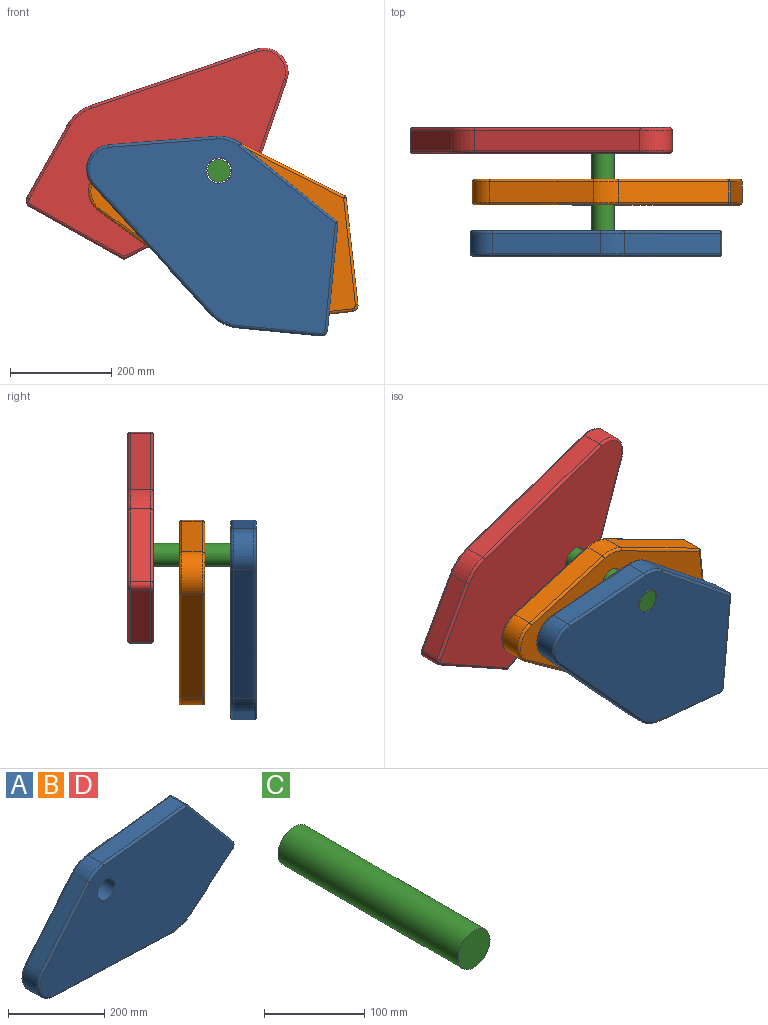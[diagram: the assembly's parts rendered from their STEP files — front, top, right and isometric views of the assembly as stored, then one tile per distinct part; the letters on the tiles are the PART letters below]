
ASSEMBLY  parts=4 mates=3
PART A: 33 faces, bbox 583.2x50.8x314.1 mm
  f0: plane 568.09x297.13mm, normal (0,-1,0), area 117364mm2, adj f10,f11,f12,f13,f14,f15,f16,f17
  f1: plane 568.09x297.13mm, normal (0,1,0), area 117364mm2, adj f10,f19,f20,f21,f22,f23,f24,f25
  f2: plane 163.02x136.69mm, normal (-0.77,0,0.64), area 8646mm2, adj f3,f9,f11,f19
  f3: cylinder r=48.03mm len=78.85mm, axis (0,1,0), area 4357.3mm2, adj f2,f4,f12,f20
  f4: plane 344.79x40.64mm, normal (-0.04,0,-1), area 14021.6mm2, adj f3,f5,f14,f22
  f5: cylinder r=83.11mm len=56.42mm, axis (0,1,0), area 2480mm2, adj f4,f6,f16,f24
  f6: plane 126.2x105.89mm, normal (0.64,0,-0.77), area 6695mm2, adj f5,f18,f26,f28
  f7: plane 162.25x136.14mm, normal (0.77,0,0.64), area 8607.4mm2, adj f17,f25,f28,f31
  f8: plane 242.51x40.64mm, normal (-0.12,0,0.99), area 9925.6mm2, adj f9,f15,f23,f31
  f9: cylinder r=68.26mm len=44.21mm, axis (0,1,0), area 2092.1mm2, adj f2,f8,f13,f21
  f10: cylinder r=25.4mm len=50.8mm, axis (0,-1,0), area 8107.3mm2, adj f0,f1
  f11: cylinder r=5.08mm len=166.29mm, axis (0.64,0,0.77), area 1697.6mm2, adj f0,f2,f12,f13
  f12: torus R=42.95mm, axis (0,-1,0), area 822.7mm2, adj f0,f3,f11,f14
  f13: torus R=63.18mm, axis (0,-1,0), area 399.7mm2, adj f0,f9,f11,f15
  f14: cylinder r=5.08mm len=344.98mm, axis (-1,0,0.04), area 2753.1mm2, adj f0,f4,f12,f16
  f15: cylinder r=5.08mm len=243.11mm, axis (0.99,0,0.12), area 1948.9mm2, adj f0,f8,f13,f32
  f16: torus R=78.03mm, axis (0,-1,0), area 476.1mm2, adj f0,f5,f14,f18
  f17: cylinder r=5.08mm len=165.51mm, axis (0.64,0,-0.77), area 1690.1mm2, adj f0,f7,f27,f32
  f18: cylinder r=5.08mm len=129.46mm, axis (-0.77,0,-0.64), area 1314.6mm2, adj f0,f6,f16,f27
  f19: cylinder r=5.08mm len=166.29mm, axis (-0.64,0,-0.77), area 1697.6mm2, adj f1,f2,f20,f21
  f20: torus R=42.95mm, axis (0,-1,0), area 822.7mm2, adj f1,f3,f19,f22
  f21: torus R=63.18mm, axis (0,-1,0), area 399.7mm2, adj f1,f9,f19,f23
  f22: cylinder r=5.08mm len=344.98mm, axis (1,0,-0.04), area 2753.1mm2, adj f1,f4,f20,f24
  f23: cylinder r=5.08mm len=243.11mm, axis (-0.99,0,-0.12), area 1948.9mm2, adj f1,f8,f21,f30
  f24: torus R=78.03mm, axis (0,-1,0), area 476.1mm2, adj f1,f5,f22,f26
  f25: cylinder r=5.08mm len=165.51mm, axis (-0.64,0,0.77), area 1690.1mm2, adj f1,f7,f29,f30
  f26: cylinder r=5.08mm len=129.46mm, axis (0.77,0,0.64), area 1314.6mm2, adj f1,f6,f24,f29
  f27: torus R=7.62mm, axis (0,-1,0), area 136mm2, adj f0,f17,f18,f28
  f28: cylinder r=12.7mm len=40.64mm, axis (0,1,0), area 810.7mm2, adj f6,f7,f27,f29
  f29: torus R=7.62mm, axis (0,-1,0), area 136mm2, adj f1,f25,f26,f28
  f30: sphere r=5.08mm, area 25.6mm2, adj f23,f25,f31
  f31: cylinder r=5.08mm len=40.64mm, axis (0,-1,0), area 204.7mm2, adj f7,f8,f30,f32
  f32: sphere r=5.08mm, area 25.6mm2, adj f15,f17,f31
PART B: same geometry as A
PART C: 3 faces, bbox 45.2x254x45.2 mm
  f0: cylinder r=22.6mm len=254mm, axis (0,1,0), area 36063.5mm2, adj f1,f2
  f1: plane 45.19x45.19mm, normal (0,-1,0), area 1604.2mm2, adj f0
  f2: plane 45.19x45.19mm, normal (0,1,0), area 1604.2mm2, adj f0
PART D: same geometry as A
PLACE A rot(axis=(0,1,0),45.5deg) t=(44.88,-101.6,-227.59)mm
PLACE B rot(axis=(0,1,0),33.7deg) t=(90.66,0,-213.53)mm
PLACE C at identity fixed
PLACE D rot(axis=(0,1,0),159.1deg) t=(-226.52,101.6,49.99)mm
MATE revolute C.f0 <-> B.f9  axis (0,1,0) through (0,0,0)mm
MATE revolute D.f9 <-> C.f0  axis (0,-1,0) through (0,127,0)mm
MATE revolute A.f9 <-> C.f0  axis (0,-1,0) through (0,-127,0)mm
